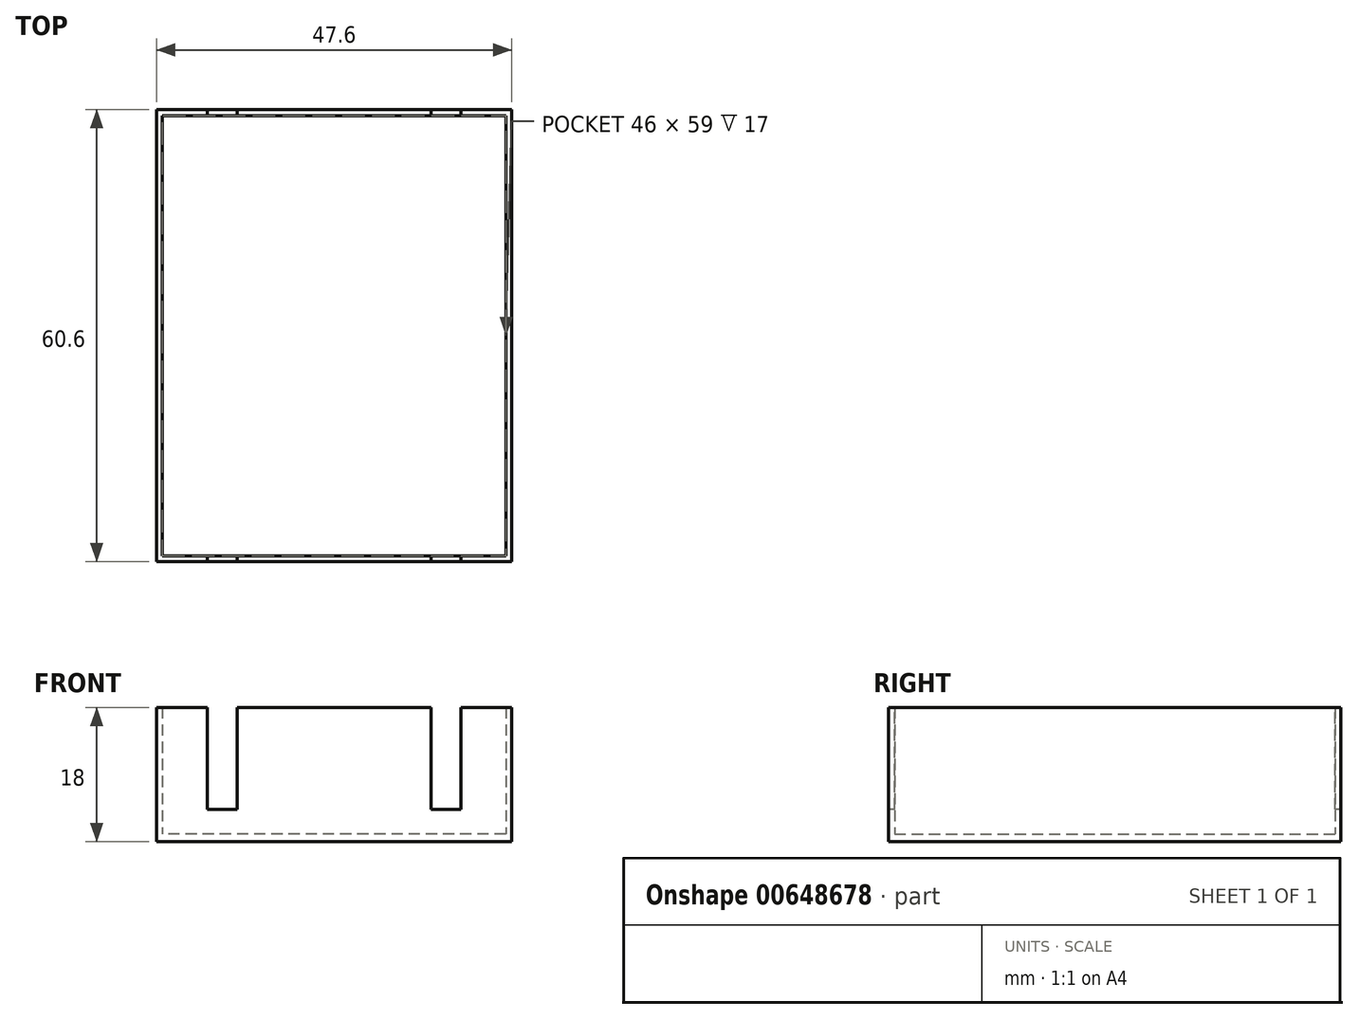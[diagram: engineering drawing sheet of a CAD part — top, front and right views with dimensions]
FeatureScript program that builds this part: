
annotation { "Feature Type Name" : "Feature", "Feature Type Description" : "" }
export const myFeature = defineFeature(function(context is Context, id is Id, definition is map)
    precondition{}
    {
        {
            var Q0;
            Q0=qCreatedBy(makeId("Top.planeOp"),FACE);
            var sketch = newSketch(context, id + "F0", { "sketchPlane" : qUnion([Q0])});
            skLineSegment(sketch, "E0.bottom", {"start": v(23, -29.5) * mm, "end": v(-23, -29.5) * mm});
            skLineSegment(sketch, "E0.top", {"start": v(23, 29.5) * mm, "end": v(-23, 29.5) * mm});
            skLineSegment(sketch, "E0.left", {"start": v(23, -29.5) * mm, "end": v(23, 29.5) * mm});
            skLineSegment(sketch, "E0.right", {"start": v(-23, -29.5) * mm, "end": v(-23, 29.5) * mm});
            skPoint(sketch, "E0.middle", {"position": v(0, 0) * mm});
            skLineSegment(sketch, "E1.0", {"start": v(23.8, 30.3) * mm, "end": v(-23.8, 30.3) * mm});
            skLineSegment(sketch, "E1.1", {"start": v(23.8, -30.3) * mm, "end": v(23.8, 30.3) * mm});
            skLineSegment(sketch, "E1.2", {"start": v(23.8, -30.3) * mm, "end": v(-23.8, -30.3) * mm});
            skLineSegment(sketch, "E1.3", {"start": v(-23.8, -30.3) * mm, "end": v(-23.8, 30.3) * mm});
            skSolve(sketch);
        }
        {
            var Q0;
            Q0=makeQuery(id+"F0.imprint","IMPRINT",FACE,{"disambiguationData":[TD([[makeQuery(id+"F0.imprint","IMPRINT",EDGE,{"derivedFrom":sQuery(id+"F0.wireOp",EDGE,"E0.bottom")}),-1.0]])]});
            extrude(context, id + "F1", {"entities" : qUnion([Q0]), "depth" : 1 * mm, "offsetDistance" : 25 * mm});
        }
        {
            var Q0;
            Q0=makeQuery(id+"F0.imprint","IMPRINT",FACE,{"disambiguationData":[TD([[makeQuery(id+"F0.imprint","IMPRINT",EDGE,{"derivedFrom":sQuery(id+"F0.wireOp",EDGE,"E0.bottom")}),1.0]])]});
            extrude(context, id + "F2", {"entities" : qUnion([Q0]), "operationType" : NewBodyOperationType.ADD, "depth" : 18 * mm, "offsetDistance" : 25 * mm});
        }
        {
            var Q0;
            Q0=makeQuery(id+"F2.opExtrude","SWEPT_FACE",FACE,{"disambiguationData":[OSD([sQuery(id+"F0.wireOp",EDGE,"E1.2")])]});
            var sketch = newSketch(context, id + "F3", { "sketchPlane" : qUnion([Q0])});
            skLineSegment(sketch, "E2.bottom", {"start": v(-13, 4.32) * mm, "end": v(-17, 4.32) * mm});
            skLineSegment(sketch, "E2.top", {"start": v(-13, 18.02) * mm, "end": v(-17, 18.02) * mm});
            skLineSegment(sketch, "E2.left", {"start": v(-13, 4.32) * mm, "end": v(-13, 18.02) * mm});
            skLineSegment(sketch, "E2.right", {"start": v(-17, 4.32) * mm, "end": v(-17, 18.02) * mm});
            skPoint(sketch, "E2.middle", {"position": v(-15, 11.17) * mm});
            skPoint(sketch, "E3.MirrorP", {"position": v(15, 11.17) * mm});
            skLineSegment(sketch, "E4.MirrorCS", {"start": v(13, 4.32) * mm, "end": v(17, 4.32) * mm});
            skLineSegment(sketch, "E5.MirrorCS", {"start": v(13, 18.02) * mm, "end": v(17, 18.02) * mm});
            skLineSegment(sketch, "E6.MirrorCS", {"start": v(13, 4.32) * mm, "end": v(13, 18.02) * mm});
            skLineSegment(sketch, "E7.MirrorCS", {"start": v(17, 4.32) * mm, "end": v(17, 18.02) * mm});
            skSolve(sketch);
        }
        {
            var Q0;
            {var subQ0=sQuery(id+"F3.wireOp",EDGE,"E2.bottom");Q0=makeQuery(id+"F3.imprint","IMPRINT",FACE,{"disambiguationData":[TD([[makeQuery(id+"F3.imprint","IMPRINT",EDGE,{"derivedFrom":subQ0}),-1.0]])]});}
            var Q1;
            {var subQ0=sQuery(id+"F3.wireOp",EDGE,"E4.MirrorCS");Q1=makeQuery(id+"F3.imprint","IMPRINT",FACE,{"disambiguationData":[TD([[makeQuery(id+"F3.imprint","IMPRINT",EDGE,{"derivedFrom":subQ0}),1.0]])]});}
            extrude(context, id + "F4", {"entities" : qUnion([Q0, Q1]), "operationType" : NewBodyOperationType.REMOVE, "oppositeDirection" : true, "depth" : 100 * mm, "offsetDistance" : 25 * mm});
        }
    });
